# Revit family: Power-ModularDevices-GEWISS-90AM-BELL_BUZZER_TRANSFORMER
name_source: partatom
category: Apparecchi elettrici
revit_build: Autodesk Revit 2016 (Build: 20161004_0715(x64)
units: mm (PartAtom-declared; Revit-internal decimal feet)

## family parameters
Condiviso = No
Host = Superficie
Mantenere orientamento annotazione = Sì
Numero OmniClass = 23.80.50.00
Punto di calcolo locali = Sì
Quota connettore circolare = Usa diametro
Taglio con vuoti quando caricato = No
Tipo di parte = Normale
Titolo OmniClass = Terminals for Power Supply

## types (1)
- GW96411 - BELL/BUZZER  230V 2M. WITH TRANSFORMER
    Barra_DIN = 5 mm  [stored 0.0164042 ft]
    Catalogue = POWER
    Catalogue Range = 90 AM
    Descrizione = BELL/BUZZER  230V 2M. WITH TRANSFORMER
    EAN code = 8011564063693
    Electrocod = 140
    IDF = 5f240de2-d4ec-4ff8-8fb3-71f135fe2d75
    IDT = a33a8038-7a60-4eae-8e2e-6ed17951036c
    Immagine tipo = GW96411.jpg
    Modello = GW96411
    No. Chorus modules = 2
    No. of modules EN 50022 = 2
    Numero di poli = 1
    Power loss = 3,8VA
    Produttore = GEWISS S.p.A.
    Prospetto di default = 1219 mm
    Rated voltage = 230V
    SEO = Combined device
    Spostamento_x = -3000 mm  [stored -9.84252 ft]
    Technical sheet = https://www.gewiss.com
    URL = https://www.gewiss.com
    Version file RFA = 18.0
    carico = Altro
    potenza in watt = 0 V

note: [stored X ft] marks values corroborated as IEEE doubles in the binary element streams (Revit-internal decimal feet)
